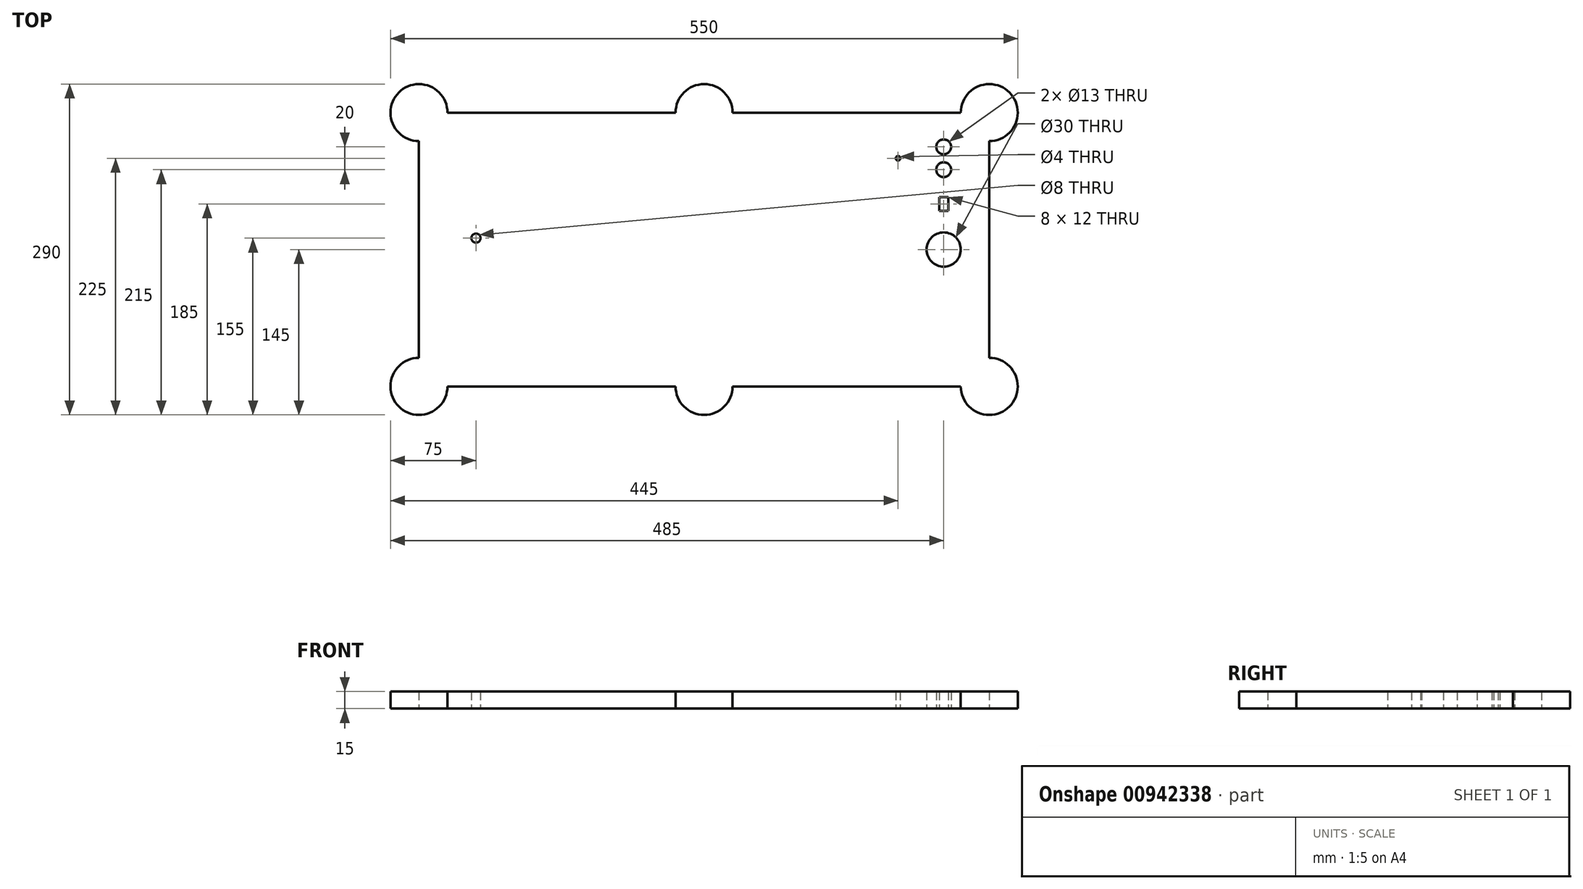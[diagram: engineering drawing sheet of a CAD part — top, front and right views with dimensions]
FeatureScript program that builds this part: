
annotation { "Feature Type Name" : "Feature", "Feature Type Description" : "" }
export const myFeature = defineFeature(function(context is Context, id is Id, definition is map)
    precondition{}
    {
        {
            var Q0;
            Q0=qCreatedBy(makeId("Top.planeOp"),FACE);
            var sketch = newSketch(context, id + "F0", { "sketchPlane" : qUnion([Q0])});
            skLineSegment(sketch, "E0.bottom", {"start": v(-120, 250) * mm, "end": v(120, 250) * mm});
            skLineSegment(sketch, "E0.top", {"start": v(-120, -250) * mm, "end": v(120, -250) * mm});
            skLineSegment(sketch, "E0.left", {"start": v(-120, 250) * mm, "end": v(-120, -250) * mm});
            skLineSegment(sketch, "E0.right", {"start": v(120, 250) * mm, "end": v(120, -250) * mm});
            skCircle(sketch, "E1", {"center": v(-120, 250) * mm, "radius": 25 * mm});
            skCircle(sketch, "E2", {"center": v(120, 250) * mm, "radius": 25 * mm});
            skCircle(sketch, "E3", {"center": v(120, 0) * mm, "radius": 25 * mm});
            skCircle(sketch, "E4", {"center": v(-120, 0) * mm, "radius": 25 * mm});
            skCircle(sketch, "E5", {"center": v(-120, -250) * mm, "radius": 25 * mm});
            skCircle(sketch, "E6", {"center": v(120, -250) * mm, "radius": 25 * mm});
            skSolve(sketch);
        }
        {
            var Q0;
            Q0 = qSketchRegion(id + "F0", true);
            extrude(context, id + "F1", {"entities" : qUnion([Q0]), "depth" : 15 * mm, "offsetDistance" : 25 * mm});
        }
        {
            var Q0;
            Q0=makeQuery(id+"F1.opExtrude","CAP_FACE",FACE,{"disambiguationData":[OSD([sQuery(id+"F0.wireOp",EDGE,"E0.bottom"),sQuery(id+"F0.wireOp",EDGE,"E0.top"),sQuery(id+"F0.wireOp",EDGE,"E0.left"),sQuery(id+"F0.wireOp",EDGE,"E0.right"),sQuery(id+"F0.wireOp",EDGE,"E1"),sQuery(id+"F0.wireOp",EDGE,"E2"),sQuery(id+"F0.wireOp",EDGE,"E3"),sQuery(id+"F0.wireOp",EDGE,"E4"),sQuery(id+"F0.wireOp",EDGE,"E5"),sQuery(id+"F0.wireOp",EDGE,"E6")])],"isStart":true});
            var sketch = newSketch(context, id + "F2", { "sketchPlane" : qUnion([Q0])});
            skCircle(sketch, "E7", {"center": v(0, -210) * mm, "radius": 15 * mm});
            skPoint(sketch, "E7.centerSnap0", {"position": v(0, -250) * mm});
            skLineSegment(sketch, "E8.bottom", {"start": v(-34, -214) * mm, "end": v(-46, -214) * mm});
            skLineSegment(sketch, "E8.top", {"start": v(-34, -206) * mm, "end": v(-46, -206) * mm});
            skLineSegment(sketch, "E8.left", {"start": v(-34, -214) * mm, "end": v(-34, -206) * mm});
            skLineSegment(sketch, "E8.right", {"start": v(-46, -214) * mm, "end": v(-46, -206) * mm});
            skPoint(sketch, "E8.middle", {"position": v(-40, -210) * mm});
            skCircle(sketch, "E9", {"center": v(-70, -210) * mm, "radius": 6.5 * mm});
            skPoint(sketch, "E9.centerSnap0", {"position": v(-46, -210) * mm});
            skCircle(sketch, "E10", {"center": v(-90, -210) * mm, "radius": 6.5 * mm});
            skCircle(sketch, "E11", {"center": v(-10, 200) * mm, "radius": 4 * mm});
            skCircle(sketch, "E12", {"center": v(-80, -170) * mm, "radius": 2 * mm});
            skSolve(sketch);
        }
        {
            var Q0;
            Q0 = qSketchRegion(id + "F2", true);
            extrude(context, id + "F3", {"entities" : qUnion([Q0]), "operationType" : NewBodyOperationType.REMOVE, "oppositeDirection" : true, "depth" : 40 * mm, "offsetDistance" : 25 * mm});
        }
        {
            var Q0;
            Q0=makeQuery(id+"F1.opExtrude","SWEPT_BODY",BODY,{"disambiguationData":[OSD([sQuery(id+"F0.wireOp",EDGE,"E0.bottom"),sQuery(id+"F0.wireOp",EDGE,"E0.top"),sQuery(id+"F0.wireOp",EDGE,"E0.left"),sQuery(id+"F0.wireOp",EDGE,"E0.right"),sQuery(id+"F0.wireOp",EDGE,"E1"),sQuery(id+"F0.wireOp",EDGE,"E2"),sQuery(id+"F0.wireOp",EDGE,"E3"),sQuery(id+"F0.wireOp",EDGE,"E4"),sQuery(id+"F0.wireOp",EDGE,"E5"),sQuery(id+"F0.wireOp",EDGE,"E6")])]});
            var Q1;
            Q1=qCreatedBy(makeId("Origin.pointOp"),VERTEX);
            var Q2;
            Q2=makeQuery(id+"F1.opExtrude","SWEPT_EDGE",EDGE,{"disambiguationData":[OSD([sQuery(id+"F0.wireOp",EDGE,"E0.left"),sQuery(id+"F0.wireOp",EDGE,"E5")])]});
            transform(context, id + "F4", {"entities" : qUnion([Q0]), "transformType" : TransformType.ROTATION, "transformAxis" : qUnion([Q2]), "angle" : 90 * degree, "makeCopy" : false});
        }
    });
